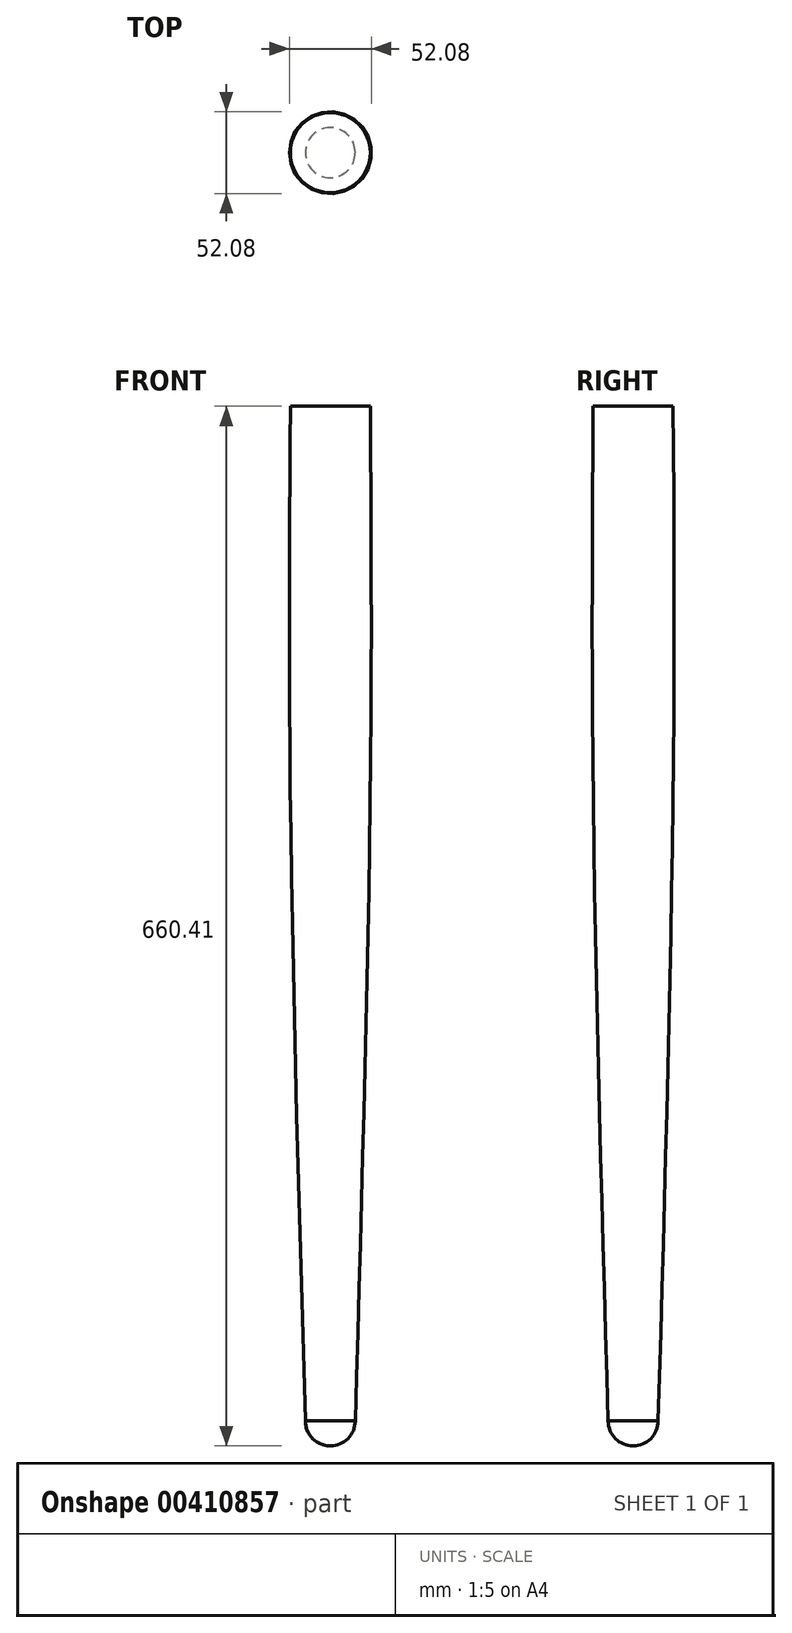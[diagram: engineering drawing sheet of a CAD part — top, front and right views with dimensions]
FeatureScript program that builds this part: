
annotation { "Feature Type Name" : "Feature", "Feature Type Description" : "" }
export const myFeature = defineFeature(function(context is Context, id is Id, definition is map)
    precondition{}
    {
        {
            var Q0;
            Q0=qCreatedBy(makeId("Front.planeOp"),FACE);
            var sketch = newSketch(context, id + "F0", { "sketchPlane" : qUnion([Q0])});
            skLineSegment(sketch, "E0", {"start": v(0, 644.53) * mm, "end": v(-25.4, 644.53) * mm});
            skArc(sketch, "E1", {"start": v(-15.88, 0) * mm, "mid": v(-11.23, -11.23) * mm, "end": v(0, -15.88) * mm});
            skLineSegment(sketch, "E2", {"start": v(0, -15.87) * mm, "end": v(0, 644.53) * mm});
            skLineSegment(sketch, "E3", {"start": v(-207.59, 396.88) * mm, "end": v(187.9, 396.88) * mm, "construction": true});
            skFitSpline(sketch, "E4", {"points": [v(-25.4, 644.53) * mm, v(-25.4, 396.88) * mm, v(-15.88, 0) * mm], "startDerivative": vector(-3.76, -528.3) * mm, "endDerivative": vector(21.81, -752) * mm});
            skSolve(sketch);
        }
        {
            var Q0;
            Q0=makeQuery(id+"F0.imprint","IMPRINT",FACE,{"disambiguationData":[TD([[makeQuery(id+"F0.imprint","IMPRINT",EDGE,{"derivedFrom":sQuery(id+"F0.wireOp",EDGE,"E0")}),1.0]])]});
            var Q1;
            Q1=sQuery(id+"F0.wireOp",EDGE,"E2");
            revolve(context, id + "F1", {"entities" : qUnion([Q0]), "axis" : qUnion([Q1]), "revolveType" : RevolveType.FULL});
        }
    });
